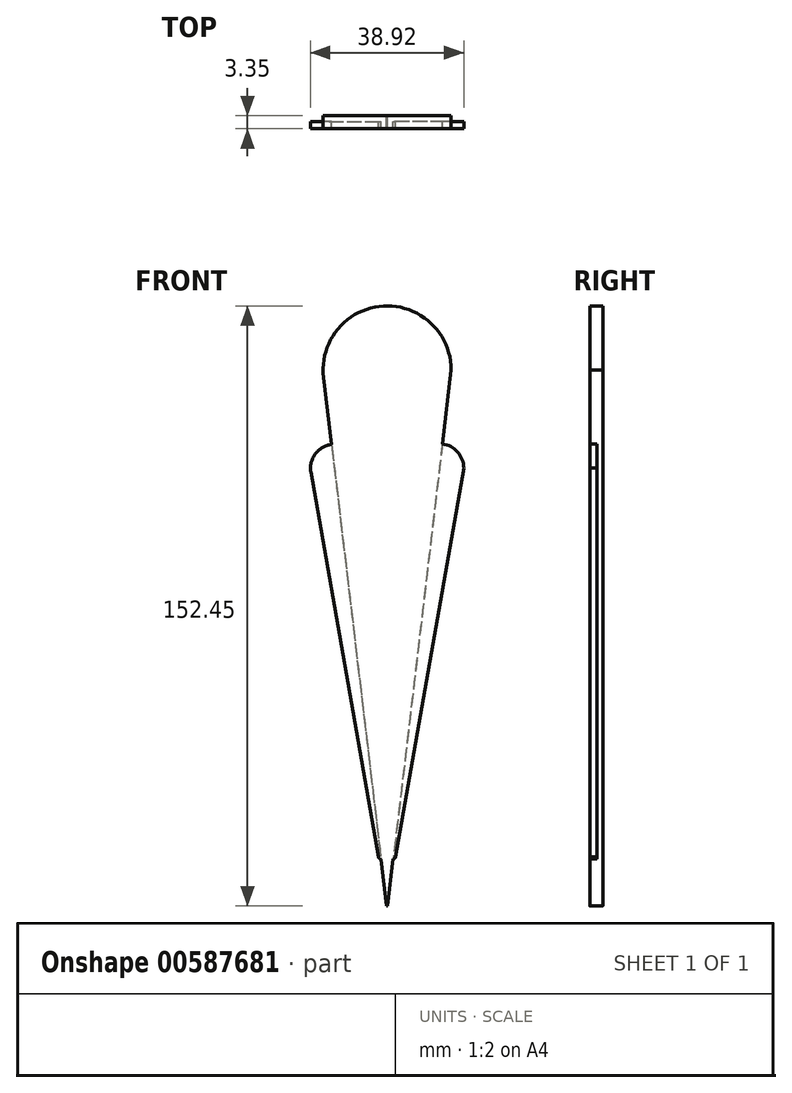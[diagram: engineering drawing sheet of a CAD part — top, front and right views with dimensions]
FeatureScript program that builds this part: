
annotation { "Feature Type Name" : "Feature", "Feature Type Description" : "" }
export const myFeature = defineFeature(function(context is Context, id is Id, definition is map)
    precondition{}
    {
        {
            var Q0;
            Q0=qCreatedBy(makeId("Front.planeOp"),FACE);
            var sketch = newSketch(context, id + "F0", { "sketchPlane" : qUnion([Q0])});
            skArc(sketch, "E0", {"start": v(16.26, 59.95) * mm, "mid": v(-0.96, 76.18) * mm, "end": v(-16.14, 58.03) * mm});
            skPoint(sketch, "E1.center.orphan", {"position": v(0, -70.11) * mm});
            skPoint(sketch, "E2.start.orphan", {"position": v(1.36, -70.11) * mm});
            skArc(sketch, "E3", {"start": v(-0.14, -76.22) * mm, "mid": v(0, -76.24) * mm, "end": v(0.14, -76.22) * mm});
            skLineSegment(sketch, "E4", {"start": v(-16.14, 58.03) * mm, "end": v(-0.14, -76.22) * mm});
            skLineSegment(sketch, "E5", {"start": v(16.26, 59.95) * mm, "end": v(0.14, -76.22) * mm});
            skArc(sketch, "E6", {"start": v(19.47, 35) * mm, "mid": v(17.91, 39.1) * mm, "end": v(14.03, 41.12) * mm});
            skArc(sketch, "E7", {"start": v(-14.11, 41) * mm, "mid": v(-18.26, 38.6) * mm, "end": v(-19.36, 33.95) * mm});
            skLineSegment(sketch, "E8", {"start": v(2.18, -63.77) * mm, "end": v(2.17, -63.77) * mm});
            skArc(sketch, "E9", {"start": v(-2.21, -63.77) * mm, "mid": v(-2.02, -64.21) * mm, "end": v(-1.56, -64.36) * mm});
            skPoint(sketch, "E10.trimOffspring.end.orphan", {"position": v(-1.62, -63.85) * mm});
            skLineSegment(sketch, "E11", {"start": v(-19.36, 33.95) * mm, "end": v(-2.21, -63.77) * mm});
            skLineSegment(sketch, "E12.trimOffspring", {"start": v(-1.62, -63.77) * mm, "end": v(-1.63, -63.77) * mm});
            skArc(sketch, "E13", {"start": v(1.55, -64.32) * mm, "mid": v(1.98, -64.19) * mm, "end": v(2.17, -63.77) * mm});
            skLineSegment(sketch, "E14", {"start": v(19.47, 35) * mm, "end": v(2.16, -63.87) * mm});
            skSolve(sketch);
        }
        {
            var Q0;
            {var subQ3=sQuery(id+"F0.wireOp",EDGE,"E0");Q0=makeQuery(id+"F0.imprint","IMPRINT",FACE,{"disambiguationData":[TD([[makeQuery(id+"F0.imprint","IMPRINT",EDGE,{"derivedFrom":subQ3}),1.0]])]});}
            extrude(context, id + "F1", {"entities" : qUnion([Q0]), "depth" : 1.78 * mm, "offsetDistance" : 25.4 * mm});
        }
        {
            var Q0;
            Q0=makeQuery(id+"F1.opExtrude","CAP_FACE",FACE,{"disambiguationData":[OSD([sQuery(id+"F0.wireOp",EDGE,"E0"),sQuery(id+"F0.wireOp",EDGE,"E3"),sQuery(id+"F0.wireOp",EDGE,"E4"),sQuery(id+"F0.wireOp",EDGE,"E5")])],"isStart":true});
            extrude(context, id + "F2", {"entities" : qUnion([Q0]), "operationType" : NewBodyOperationType.ADD, "depth" : 1.57 * mm, "offsetDistance" : 25.4 * mm});
        }
        {
            var Q0;
            {var subQ6=sQuery(id+"F0.wireOp",EDGE,"E6");Q0=makeQuery(id+"F0.imprint","IMPRINT",FACE,{"disambiguationData":[TD([[makeQuery(id+"F0.imprint","IMPRINT",EDGE,{"derivedFrom":subQ6}),1.0]])]});}
            var Q1;
            {var subQ1=sQuery(id+"F0.wireOp",EDGE,"E7");Q1=makeQuery(id+"F0.imprint","IMPRINT",FACE,{"disambiguationData":[TD([[makeQuery(id+"F0.imprint","IMPRINT",EDGE,{"derivedFrom":subQ1}),1.0]])]});}
            extrude(context, id + "F3", {"entities" : qUnion([Q0, Q1]), "operationType" : NewBodyOperationType.ADD, "depth" : 1.78 * mm, "offsetDistance" : 25.4 * mm});
        }
    });
